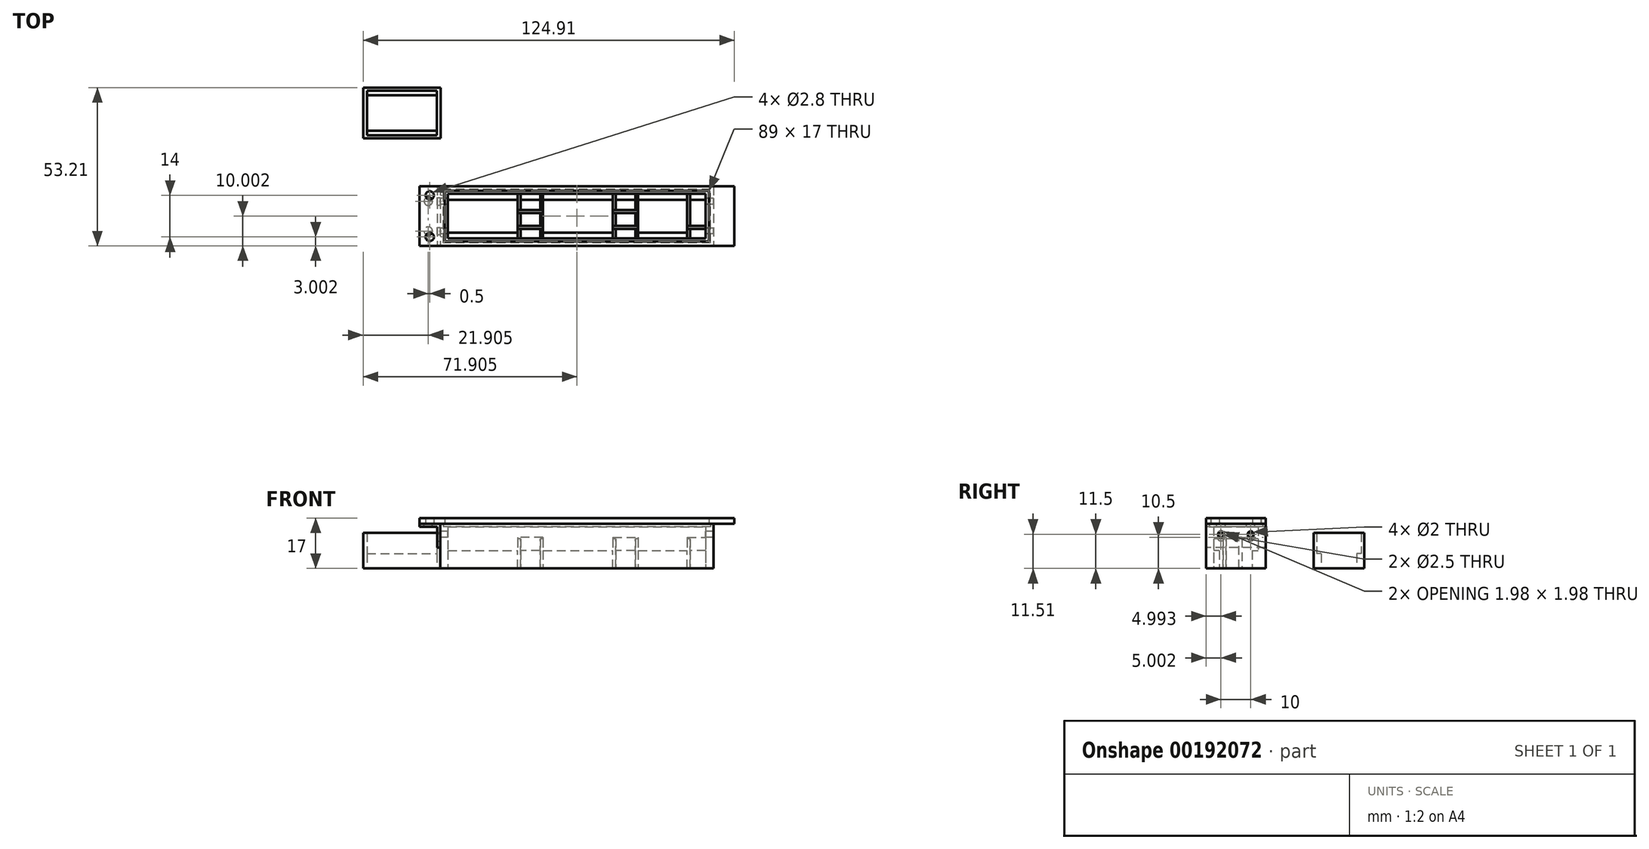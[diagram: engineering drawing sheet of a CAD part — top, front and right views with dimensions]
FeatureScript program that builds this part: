
annotation { "Feature Type Name" : "Feature", "Feature Type Description" : "" }
export const myFeature = defineFeature(function(context is Context, id is Id, definition is map)
    precondition{}
    {
        {
            var Q0;
            Q0=qCreatedBy(makeId("Top.planeOp"),FACE);
            var sketch = newSketch(context, id + "F0", { "sketchPlane" : qUnion([Q0])});
            skLineSegment(sketch, "E0.bottom", {"start": v(-43.66, -37.07) * mm, "end": v(-67.16, -37.07) * mm});
            skLineSegment(sketch, "E0.top", {"start": v(-43.66, -22.07) * mm, "end": v(-67.16, -22.07) * mm});
            skLineSegment(sketch, "E0.left", {"start": v(-43.66, -37.07) * mm, "end": v(-43.66, -22.07) * mm});
            skLineSegment(sketch, "E0.right", {"start": v(-67.16, -37.07) * mm, "end": v(-67.16, -22.07) * mm});
            skPoint(sketch, "E0.middle", {"position": v(-55.4, -29.57) * mm});
            skLineSegment(sketch, "E1.bottom", {"start": v(-42.4, -38.07) * mm, "end": v(-68.4, -38.07) * mm});
            skLineSegment(sketch, "E1.top", {"start": v(-42.4, -21.07) * mm, "end": v(-68.4, -21.07) * mm});
            skLineSegment(sketch, "E1.left", {"start": v(-42.4, -38.07) * mm, "end": v(-42.4, -21.07) * mm});
            skLineSegment(sketch, "E1.right", {"start": v(-68.4, -38.07) * mm, "end": v(-68.4, -21.07) * mm});
            skSolve(sketch);
        }
        {
            var Q0;
            Q0 = qSketchRegion(id + "F0", true);
            extrude(context, id + "F1", {"entities" : qUnion([Q0]), "depth" : 12 * mm});
        }
        {
            var Q0;
            Q0=qCreatedBy(makeId("Top.planeOp"),FACE);
            var sketch = newSketch(context, id + "F2", { "sketchPlane" : qUnion([Q0])});
            skLineSegment(sketch, "E2.bottom", {"start": v(-67.16, -22.07) * mm, "end": v(-43.66, -22.07) * mm});
            skLineSegment(sketch, "E2.top", {"start": v(-67.16, -23.57) * mm, "end": v(-43.66, -23.57) * mm});
            skLineSegment(sketch, "E2.left", {"start": v(-67.16, -22.07) * mm, "end": v(-67.16, -23.57) * mm});
            skLineSegment(sketch, "E2.right", {"start": v(-43.66, -22.07) * mm, "end": v(-43.66, -23.57) * mm});
            skLineSegment(sketch, "E3.bottom", {"start": v(-67.16, -35.57) * mm, "end": v(-43.66, -35.57) * mm});
            skLineSegment(sketch, "E3.top", {"start": v(-67.16, -37.07) * mm, "end": v(-43.66, -37.07) * mm});
            skLineSegment(sketch, "E3.left", {"start": v(-67.16, -35.57) * mm, "end": v(-67.16, -37.07) * mm});
            skLineSegment(sketch, "E3.right", {"start": v(-43.66, -35.57) * mm, "end": v(-43.66, -37.07) * mm});
            skSolve(sketch);
        }
        {
            var Q0;
            Q0 = qSketchRegion(id + "F2", true);
            extrude(context, id + "F3", {"entities" : qUnion([Q0]), "operationType" : NewBodyOperationType.ADD, "depth" : 5 * mm});
        }
        {
            var Q0;
            Q0=qCreatedBy(makeId("Top.planeOp"),FACE);
            var sketch = newSketch(context, id + "F4", { "sketchPlane" : qUnion([Q0])});
            skLineSegment(sketch, "E4.bottom", {"start": v(48.5, -73.28) * mm, "end": v(-41.5, -73.28) * mm});
            skLineSegment(sketch, "E4.top", {"start": v(48.5, -55.28) * mm, "end": v(-41.5, -55.28) * mm});
            skLineSegment(sketch, "E4.left", {"start": v(48.5, -73.28) * mm, "end": v(48.5, -55.28) * mm});
            skLineSegment(sketch, "E4.right", {"start": v(-41.5, -73.28) * mm, "end": v(-41.5, -55.28) * mm});
            skPoint(sketch, "E4.middle", {"position": v(3.5, -64.28) * mm});
            skLineSegment(sketch, "E5.bottom", {"start": v(-16.38, -71.78) * mm, "end": v(-39.88, -71.78) * mm});
            skLineSegment(sketch, "E5.top", {"start": v(-16.38, -56.78) * mm, "end": v(-39.88, -56.78) * mm});
            skLineSegment(sketch, "E5.left", {"start": v(-16.38, -71.78) * mm, "end": v(-16.38, -56.78) * mm});
            skLineSegment(sketch, "E5.right", {"start": v(-39.88, -71.78) * mm, "end": v(-39.88, -56.78) * mm});
            skPoint(sketch, "E5.middle", {"position": v(-28.13, -64.28) * mm});
            skLineSegment(sketch, "E6.bottom", {"start": v(15.62, -71.78) * mm, "end": v(-7.88, -71.78) * mm});
            skLineSegment(sketch, "E6.top", {"start": v(15.62, -56.78) * mm, "end": v(-7.88, -56.78) * mm});
            skLineSegment(sketch, "E6.left", {"start": v(15.62, -71.78) * mm, "end": v(15.62, -56.78) * mm});
            skLineSegment(sketch, "E6.right", {"start": v(-7.88, -71.78) * mm, "end": v(-7.88, -56.78) * mm});
            skPoint(sketch, "E6.middle", {"position": v(3.87, -64.28) * mm});
            skLineSegment(sketch, "E7.bottom", {"start": v(24.12, -71.78) * mm, "end": v(40.62, -71.78) * mm});
            skLineSegment(sketch, "E7.top", {"start": v(24.12, -56.78) * mm, "end": v(40.62, -56.78) * mm});
            skLineSegment(sketch, "E7.left", {"start": v(24.12, -71.78) * mm, "end": v(24.12, -56.78) * mm});
            skLineSegment(sketch, "E7.right", {"start": v(40.62, -71.78) * mm, "end": v(40.62, -56.78) * mm});
            skPoint(sketch, "E7.middle", {"position": v(32.37, -64.28) * mm});
            skLineSegment(sketch, "E8.bottom", {"start": v(-17.13, -84.92) * mm, "end": v(-39.13, -84.92) * mm, "construction": true});
            skLineSegment(sketch, "E8.top", {"start": v(-17.13, -81.02) * mm, "end": v(-39.13, -81.02) * mm, "construction": true});
            skLineSegment(sketch, "E8.left", {"start": v(-17.13, -84.92) * mm, "end": v(-17.13, -81.02) * mm, "construction": true});
            skLineSegment(sketch, "E8.right", {"start": v(-39.13, -84.92) * mm, "end": v(-39.13, -81.02) * mm, "construction": true});
            skPoint(sketch, "E8.middle", {"position": v(-28.13, -82.97) * mm});
            skLineSegment(sketch, "E9.bottom", {"start": v(14.87, -85.01) * mm, "end": v(-7.13, -85.01) * mm, "construction": true});
            skLineSegment(sketch, "E9.top", {"start": v(14.87, -80.93) * mm, "end": v(-7.13, -80.93) * mm, "construction": true});
            skLineSegment(sketch, "E9.left", {"start": v(14.87, -85.01) * mm, "end": v(14.87, -80.93) * mm, "construction": true});
            skLineSegment(sketch, "E9.right", {"start": v(-7.13, -85.01) * mm, "end": v(-7.13, -80.93) * mm, "construction": true});
            skPoint(sketch, "E9.middle", {"position": v(3.87, -82.97) * mm});
            skPoint(sketch, "E9.middle.positionSnap0", {"position": v(-17.13, -82.97) * mm});
            skPoint(sketch, "E9.centerSnap0", {"position": v(-17.13, -82.97) * mm});
            skLineSegment(sketch, "E10.bottom", {"start": v(39.87, -85.01) * mm, "end": v(24.87, -85.01) * mm, "construction": true});
            skLineSegment(sketch, "E10.top", {"start": v(39.87, -80.93) * mm, "end": v(24.87, -80.93) * mm, "construction": true});
            skLineSegment(sketch, "E10.left", {"start": v(39.87, -85.01) * mm, "end": v(39.87, -80.93) * mm, "construction": true});
            skLineSegment(sketch, "E10.right", {"start": v(24.87, -85.01) * mm, "end": v(24.87, -80.93) * mm, "construction": true});
            skPoint(sketch, "E10.middle", {"position": v(32.37, -82.97) * mm});
            skPoint(sketch, "E10.middle.positionSnap1", {"position": v(14.87, -82.97) * mm});
            skPoint(sketch, "E10.centerSnap1", {"position": v(14.87, -82.97) * mm});
            skLineSegment(sketch, "E11.bottom", {"start": v(-15.38, -56.78) * mm, "end": v(-8.88, -56.78) * mm});
            skLineSegment(sketch, "E11.top", {"start": v(-15.38, -71.78) * mm, "end": v(-8.88, -71.78) * mm});
            skLineSegment(sketch, "E11.left", {"start": v(-15.38, -56.78) * mm, "end": v(-15.38, -71.78) * mm});
            skLineSegment(sketch, "E11.right", {"start": v(-8.88, -56.78) * mm, "end": v(-8.88, -71.78) * mm});
            skLineSegment(sketch, "E12.bottom", {"start": v(16.62, -56.78) * mm, "end": v(23.12, -56.78) * mm});
            skLineSegment(sketch, "E12.top", {"start": v(16.62, -71.78) * mm, "end": v(23.12, -71.78) * mm});
            skLineSegment(sketch, "E12.left", {"start": v(16.62, -56.78) * mm, "end": v(16.62, -71.78) * mm});
            skLineSegment(sketch, "E12.right", {"start": v(23.12, -56.78) * mm, "end": v(23.12, -71.78) * mm});
            skLineSegment(sketch, "E13.bottom", {"start": v(41.62, -56.78) * mm, "end": v(46.87, -56.78) * mm});
            skLineSegment(sketch, "E13.top", {"start": v(41.62, -71.78) * mm, "end": v(46.87, -71.78) * mm});
            skLineSegment(sketch, "E13.left", {"start": v(41.62, -56.78) * mm, "end": v(41.62, -71.78) * mm});
            skLineSegment(sketch, "E13.right", {"start": v(46.87, -56.78) * mm, "end": v(46.87, -71.78) * mm});
            skSolve(sketch);
        }
        {
            var Q0;
            Q0 = qSketchRegion(id + "F4", true);
            extrude(context, id + "F5", {"entities" : qUnion([Q0]), "depth" : 14 * mm});
        }
        {
            var Q0;
            Q0=makeQuery(id+"F5.opExtrude","CAP_FACE",FACE,{"disambiguationData":[OSD([sQuery(id+"F4.wireOp",EDGE,"E4.bottom"),sQuery(id+"F4.wireOp",EDGE,"E4.top"),sQuery(id+"F4.wireOp",EDGE,"E4.left"),sQuery(id+"F4.wireOp",EDGE,"E4.right"),sQuery(id+"F4.wireOp",EDGE,"E5.bottom"),sQuery(id+"F4.wireOp",EDGE,"E5.top"),sQuery(id+"F4.wireOp",EDGE,"E5.left"),sQuery(id+"F4.wireOp",EDGE,"E5.right"),sQuery(id+"F4.wireOp",EDGE,"E6.bottom"),sQuery(id+"F4.wireOp",EDGE,"E6.top"),sQuery(id+"F4.wireOp",EDGE,"E6.left"),sQuery(id+"F4.wireOp",EDGE,"E6.right"),sQuery(id+"F4.wireOp",EDGE,"E7.bottom"),sQuery(id+"F4.wireOp",EDGE,"E7.top"),sQuery(id+"F4.wireOp",EDGE,"E7.left"),sQuery(id+"F4.wireOp",EDGE,"E7.right"),sQuery(id+"F4.wireOp",EDGE,"E11.bottom"),sQuery(id+"F4.wireOp",EDGE,"E11.top"),sQuery(id+"F4.wireOp",EDGE,"E11.left"),sQuery(id+"F4.wireOp",EDGE,"E11.right"),sQuery(id+"F4.wireOp",EDGE,"E12.bottom"),sQuery(id+"F4.wireOp",EDGE,"E12.top"),sQuery(id+"F4.wireOp",EDGE,"E12.left"),sQuery(id+"F4.wireOp",EDGE,"E12.right"),sQuery(id+"F4.wireOp",EDGE,"E13.bottom"),sQuery(id+"F4.wireOp",EDGE,"E13.top"),sQuery(id+"F4.wireOp",EDGE,"E13.left"),sQuery(id+"F4.wireOp",EDGE,"E13.right")])],"isStart":false});
            var sketch = newSketch(context, id + "F6", { "sketchPlane" : qUnion([Q0])});
            skLineSegment(sketch, "E14.bottom", {"start": v(-20.31, -71.78) * mm, "end": v(43.02, -71.78) * mm});
            skLineSegment(sketch, "E14.top", {"start": v(-20.31, -56.78) * mm, "end": v(43.02, -56.78) * mm});
            skLineSegment(sketch, "E14.left", {"start": v(-20.31, -71.78) * mm, "end": v(-20.31, -56.78) * mm});
            skLineSegment(sketch, "E14.right", {"start": v(43.02, -71.78) * mm, "end": v(43.02, -56.78) * mm});
            skSolve(sketch);
        }
        {
            var Q0;
            Q0 = qSketchRegion(id + "F6", true);
            extrude(context, id + "F7", {"entities" : qUnion([Q0]), "operationType" : NewBodyOperationType.REMOVE, "oppositeDirection" : true, "depth" : 4 * mm});
        }
        {
            var Q0;
            Q0=qCreatedBy(makeId("Top.planeOp"),FACE);
            var sketch = newSketch(context, id + "F8", { "sketchPlane" : qUnion([Q0])});
            skLineSegment(sketch, "E15.bottom", {"start": v(46.87, -58.78) * mm, "end": v(-39.88, -58.78) * mm});
            skLineSegment(sketch, "E15.top", {"start": v(46.87, -56.78) * mm, "end": v(-39.88, -56.78) * mm});
            skLineSegment(sketch, "E15.left", {"start": v(46.87, -58.78) * mm, "end": v(46.87, -56.78) * mm});
            skLineSegment(sketch, "E15.right", {"start": v(-39.88, -58.78) * mm, "end": v(-39.88, -56.78) * mm});
            skPoint(sketch, "E15.middle", {"position": v(3.5, -57.78) * mm});
            skLineSegment(sketch, "E16.bottom", {"start": v(-39.88, -69.78) * mm, "end": v(-16.38, -69.78) * mm});
            skLineSegment(sketch, "E16.top", {"start": v(-39.88, -71.78) * mm, "end": v(-16.38, -71.78) * mm});
            skLineSegment(sketch, "E16.left", {"start": v(-39.88, -69.78) * mm, "end": v(-39.88, -71.78) * mm});
            skLineSegment(sketch, "E16.right", {"start": v(-16.38, -69.78) * mm, "end": v(-16.38, -71.78) * mm});
            skLineSegment(sketch, "E17.bottom", {"start": v(-7.88, -69.78) * mm, "end": v(15.62, -69.78) * mm});
            skLineSegment(sketch, "E17.top", {"start": v(-7.88, -71.78) * mm, "end": v(15.62, -71.78) * mm});
            skLineSegment(sketch, "E17.left", {"start": v(-7.88, -69.78) * mm, "end": v(-7.88, -71.78) * mm});
            skLineSegment(sketch, "E17.right", {"start": v(15.62, -69.78) * mm, "end": v(15.62, -71.78) * mm});
            skLineSegment(sketch, "E18.bottom", {"start": v(24.12, -69.78) * mm, "end": v(40.62, -69.78) * mm});
            skLineSegment(sketch, "E18.top", {"start": v(24.12, -71.78) * mm, "end": v(40.62, -71.78) * mm});
            skLineSegment(sketch, "E18.left", {"start": v(24.12, -69.78) * mm, "end": v(24.12, -71.78) * mm});
            skLineSegment(sketch, "E18.right", {"start": v(40.62, -69.78) * mm, "end": v(40.62, -71.78) * mm});
            skSolve(sketch);
        }
        {
            var Q0;
            Q0 = qSketchRegion(id + "F8", true);
            extrude(context, id + "F9", {"entities" : qUnion([Q0]), "operationType" : NewBodyOperationType.ADD, "depth" : 6 * mm});
        }
        {
            var Q0;
            Q0=qCreatedBy(makeId("Top.planeOp"),FACE);
            var sketch = newSketch(context, id + "F10", { "sketchPlane" : qUnion([Q0])});
            skLineSegment(sketch, "E19.bottom", {"start": v(-7.88, -62.28) * mm, "end": v(-16.38, -62.28) * mm});
            skLineSegment(sketch, "E19.top", {"start": v(-7.88, -63.28) * mm, "end": v(-16.38, -63.28) * mm});
            skLineSegment(sketch, "E19.left", {"start": v(-7.88, -62.28) * mm, "end": v(-7.88, -63.28) * mm});
            skLineSegment(sketch, "E19.right", {"start": v(-16.38, -62.28) * mm, "end": v(-16.38, -63.28) * mm});
            skLineSegment(sketch, "E20.bottom", {"start": v(15.62, -62.28) * mm, "end": v(24.12, -62.28) * mm});
            skLineSegment(sketch, "E20.top", {"start": v(15.62, -63.28) * mm, "end": v(24.12, -63.28) * mm});
            skLineSegment(sketch, "E20.left", {"start": v(15.62, -62.28) * mm, "end": v(15.62, -63.28) * mm});
            skLineSegment(sketch, "E20.right", {"start": v(24.12, -62.28) * mm, "end": v(24.12, -63.28) * mm});
            skLineSegment(sketch, "E21.bottom", {"start": v(-16.38, -67.58) * mm, "end": v(-7.88, -67.58) * mm});
            skLineSegment(sketch, "E21.top", {"start": v(-16.38, -68.58) * mm, "end": v(-7.88, -68.58) * mm});
            skLineSegment(sketch, "E21.left", {"start": v(-16.38, -67.58) * mm, "end": v(-16.38, -68.58) * mm});
            skLineSegment(sketch, "E21.right", {"start": v(-7.88, -67.58) * mm, "end": v(-7.88, -68.58) * mm});
            skPoint(sketch, "E22.firstSnap0", {"position": v(-12.13, -67.58) * mm});
            skLineSegment(sketch, "E22.bottom", {"start": v(15.62, -67.58) * mm, "end": v(24.12, -67.58) * mm});
            skLineSegment(sketch, "E22.top", {"start": v(15.62, -68.58) * mm, "end": v(24.12, -68.58) * mm});
            skLineSegment(sketch, "E22.left", {"start": v(15.62, -67.58) * mm, "end": v(15.62, -68.58) * mm});
            skLineSegment(sketch, "E22.right", {"start": v(24.12, -67.58) * mm, "end": v(24.12, -68.58) * mm});
            skLineSegment(sketch, "E23.bottom", {"start": v(40.62, -67.58) * mm, "end": v(46.87, -67.58) * mm});
            skLineSegment(sketch, "E23.top", {"start": v(40.62, -68.58) * mm, "end": v(46.87, -68.58) * mm});
            skLineSegment(sketch, "E23.left", {"start": v(40.62, -67.58) * mm, "end": v(40.62, -68.58) * mm});
            skLineSegment(sketch, "E23.right", {"start": v(46.87, -67.58) * mm, "end": v(46.87, -68.58) * mm});
            skSolve(sketch);
        }
        {
            var Q0;
            Q0 = qSketchRegion(id + "F10", true);
            extrude(context, id + "F11", {"entities" : qUnion([Q0]), "operationType" : NewBodyOperationType.ADD, "depth" : 10.5 * mm});
        }
        {
            var Q0;
            Q0=qCreatedBy(makeId("Top.planeOp"),FACE);
            var sketch = newSketch(context, id + "F12", { "sketchPlane" : qUnion([Q0])});
            skLineSegment(sketch, "E24.bottom", {"start": v(-41.5, -55.28) * mm, "end": v(48.5, -55.28) * mm});
            skLineSegment(sketch, "E24.top", {"start": v(-41.5, -73.28) * mm, "end": v(48.5, -73.28) * mm});
            skLineSegment(sketch, "E24.left", {"start": v(-41.5, -55.28) * mm, "end": v(-41.5, -73.28) * mm});
            skLineSegment(sketch, "E24.right", {"start": v(48.5, -55.28) * mm, "end": v(48.5, -73.28) * mm});
            skLineSegment(sketch, "E25.bottom", {"start": v(-42.5, -54.28) * mm, "end": v(49.5, -54.28) * mm});
            skLineSegment(sketch, "E25.top", {"start": v(-42.5, -74.28) * mm, "end": v(49.5, -74.28) * mm});
            skLineSegment(sketch, "E25.left", {"start": v(-42.5, -54.28) * mm, "end": v(-42.5, -74.28) * mm});
            skLineSegment(sketch, "E25.right", {"start": v(49.5, -54.28) * mm, "end": v(49.5, -74.28) * mm});
            skSolve(sketch);
        }
        {
            var Q0;
            Q0 = qSketchRegion(id + "F12", true);
            extrude(context, id + "F13", {"entities" : qUnion([Q0]), "operationType" : NewBodyOperationType.ADD, "depth" : 15 * mm});
        }
        {
            var Q0;
            Q0=makeQuery(id+"F13.opExtrude","SWEPT_FACE",FACE,{"disambiguationData":[OSD([sQuery(id+"F12.wireOp",EDGE,"E25.left")])]});
            var sketch = newSketch(context, id + "F14", { "sketchPlane" : qUnion([Q0])});
            skCircle(sketch, "E26", {"center": v(59.28, 11.5) * mm, "radius": 1 * mm});
            skCircle(sketch, "E27", {"center": v(69.28, 11.5) * mm, "radius": 1 * mm});
            skSolve(sketch);
        }
        {
            var Q0;
            Q0 = qSketchRegion(id + "F14", true);
            extrude(context, id + "F15", {"entities" : qUnion([Q0]), "operationType" : NewBodyOperationType.REMOVE, "oppositeDirection" : true, "depth" : 100.1 * mm});
        }
        {
            var Q0;
            Q0=makeQuery(id+"F13.opExtrude","SWEPT_FACE",FACE,{"disambiguationData":[OSD([sQuery(id+"F12.wireOp",EDGE,"E25.left")])]});
            var sketch = newSketch(context, id + "F16", { "sketchPlane" : qUnion([Q0])});
            skLineSegment(sketch, "E28.bottom", {"start": v(54.28, 15) * mm, "end": v(74.28, 15) * mm});
            skLineSegment(sketch, "E28.top", {"start": v(54.28, 7) * mm, "end": v(74.28, 7) * mm});
            skLineSegment(sketch, "E28.left", {"start": v(54.28, 15) * mm, "end": v(54.28, 7) * mm});
            skLineSegment(sketch, "E28.right", {"start": v(74.28, 15) * mm, "end": v(74.28, 7) * mm});
            skCircle(sketch, "E29", {"center": v(59.28, 10.5) * mm, "radius": 1.25 * mm});
            skCircle(sketch, "E30", {"center": v(69.28, 10.5) * mm, "radius": 1.25 * mm});
            skSolve(sketch);
        }
        {
            var Q0;
            Q0 = qSketchRegion(id + "F16", true);
            extrude(context, id + "F17", {"entities" : qUnion([Q0]), "depth" : 1 * mm});
        }
        {
            var Q0;
            Q0=makeQuery(id+"F17.opExtrude","SWEPT_FACE",FACE,{"disambiguationData":[OSD([sQuery(id+"F16.wireOp",EDGE,"E28.bottom")])]});
            var sketch = newSketch(context, id + "F18", { "sketchPlane" : qUnion([Q0])});
            skLineSegment(sketch, "E31.bottom", {"start": v(-43.5, -54.28) * mm, "end": v(-49.5, -54.28) * mm});
            skLineSegment(sketch, "E31.top", {"start": v(-43.5, -74.28) * mm, "end": v(-49.5, -74.28) * mm});
            skLineSegment(sketch, "E31.left", {"start": v(-43.5, -54.28) * mm, "end": v(-43.5, -74.28) * mm});
            skLineSegment(sketch, "E31.right", {"start": v(-49.5, -54.28) * mm, "end": v(-49.5, -74.28) * mm});
            skCircle(sketch, "E32", {"center": v(-46.5, -59.28) * mm, "radius": 1.4 * mm});
            skCircle(sketch, "E33", {"center": v(-46.5, -69.28) * mm, "radius": 1.4 * mm});
            skSolve(sketch);
        }
        {
            var Q0;
            Q0 = qSketchRegion(id + "F18", true);
            extrude(context, id + "F19", {"entities" : qUnion([Q0]), "operationType" : NewBodyOperationType.ADD, "oppositeDirection" : true, "depth" : 1 * mm});
        }
        {
            var Q0;
            Q0=makeQuery(id+"F13.opExtrude","CAP_FACE",FACE,{"disambiguationData":[OSD([sQuery(id+"F12.wireOp",EDGE,"E24.bottom"),sQuery(id+"F12.wireOp",EDGE,"E24.top"),sQuery(id+"F12.wireOp",EDGE,"E24.left"),sQuery(id+"F12.wireOp",EDGE,"E24.right"),sQuery(id+"F12.wireOp",EDGE,"E25.bottom"),sQuery(id+"F12.wireOp",EDGE,"E25.top"),sQuery(id+"F12.wireOp",EDGE,"E25.left"),sQuery(id+"F12.wireOp",EDGE,"E25.right")])],"isStart":false});
            var sketch = newSketch(context, id + "F20", { "sketchPlane" : qUnion([Q0])});
            skLineSegment(sketch, "E34.bottom", {"start": v(-49.5, -54.28) * mm, "end": v(56.5, -54.28) * mm});
            skLineSegment(sketch, "E34.top", {"start": v(-49.5, -74.28) * mm, "end": v(56.5, -74.28) * mm});
            skLineSegment(sketch, "E34.left", {"start": v(-49.5, -54.28) * mm, "end": v(-49.5, -74.28) * mm});
            skLineSegment(sketch, "E34.right", {"start": v(56.5, -54.28) * mm, "end": v(56.5, -74.28) * mm});
            skLineSegment(sketch, "E35.bottom", {"start": v(-41, -55.78) * mm, "end": v(48, -55.78) * mm});
            skLineSegment(sketch, "E35.top", {"start": v(-41, -72.78) * mm, "end": v(48, -72.78) * mm});
            skLineSegment(sketch, "E35.left", {"start": v(-41, -55.78) * mm, "end": v(-41, -72.78) * mm});
            skLineSegment(sketch, "E35.right", {"start": v(48, -55.78) * mm, "end": v(48, -72.78) * mm});
            skCircle(sketch, "E36", {"center": v(-46, -57.28) * mm, "radius": 1.4 * mm});
            skCircle(sketch, "E37", {"center": v(-46, -71.28) * mm, "radius": 1.4 * mm});
            skSolve(sketch);
        }
        {
            var Q0;
            Q0 = qSketchRegion(id + "F20", true);
            extrude(context, id + "F21", {"entities" : qUnion([Q0]), "depth" : 2 * mm});
        }
    });
